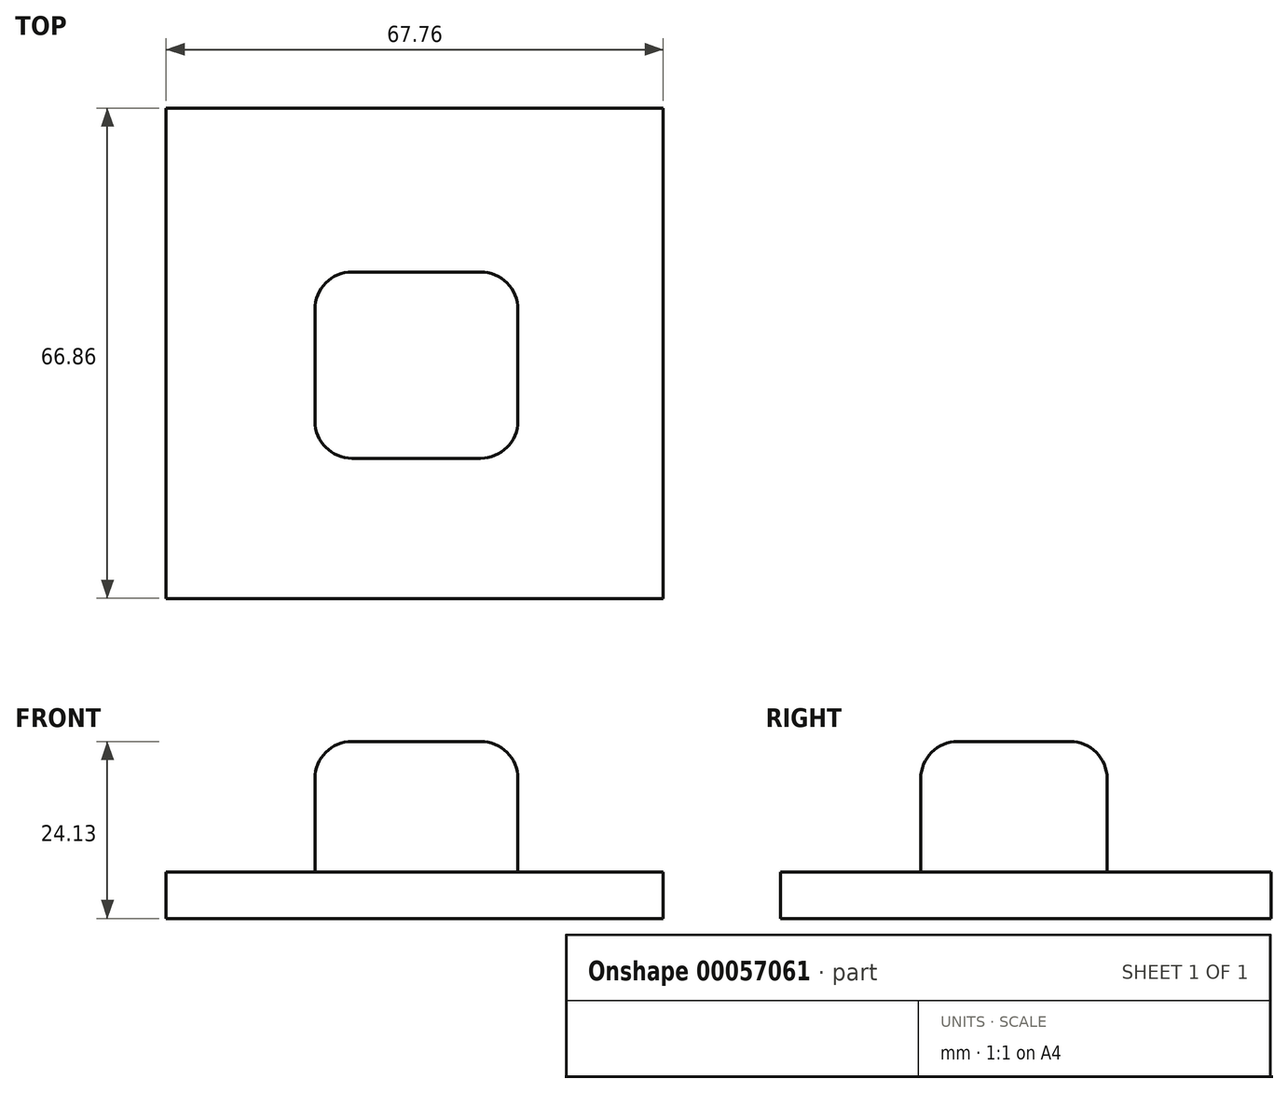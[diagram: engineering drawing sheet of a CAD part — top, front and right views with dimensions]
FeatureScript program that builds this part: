
annotation { "Feature Type Name" : "Feature", "Feature Type Description" : "" }
export const myFeature = defineFeature(function(context is Context, id is Id, definition is map)
    precondition{}
    {
        {
            var Q0;
            Q0=qCreatedBy(makeId("Top.planeOp"),FACE);
            var sketch = newSketch(context, id + "F0", { "sketchPlane" : qUnion([Q0])});
            skLineSegment(sketch, "E0.bottom", {"start": v(-35.63, 22.68) * mm, "end": v(32.13, 22.68) * mm});
            skLineSegment(sketch, "E0.top", {"start": v(-35.63, -44.18) * mm, "end": v(32.13, -44.18) * mm});
            skLineSegment(sketch, "E0.left", {"start": v(-35.63, 22.68) * mm, "end": v(-35.63, -44.18) * mm});
            skLineSegment(sketch, "E0.right", {"start": v(32.13, 22.68) * mm, "end": v(32.13, -44.18) * mm});
            skSolve(sketch);
        }
        {
            var Q0;
            Q0=makeQuery(id+"F0.imprint","IMPRINT",FACE,{"disambiguationData":[TD([[makeQuery(id+"F0.imprint","IMPRINT",EDGE,{"derivedFrom":sQuery(id+"F0.wireOp",EDGE,"E0.bottom")}),-1.0]])]});
            extrude(context, id + "F1", {"entities" : qUnion([Q0]), "depth" : 6.35 * mm});
        }
        {
            var Q0;
            Q0=makeQuery(id+"F1.opExtrude","CAP_FACE",FACE,{"disambiguationData":[OSD([sQuery(id+"F0.wireOp",EDGE,"E0.bottom"),sQuery(id+"F0.wireOp",EDGE,"E0.top"),sQuery(id+"F0.wireOp",EDGE,"E0.left"),sQuery(id+"F0.wireOp",EDGE,"E0.right")])],"isStart":false});
            var sketch = newSketch(context, id + "F2", { "sketchPlane" : qUnion([Q0])});
            skLineSegment(sketch, "E1.bottom", {"start": v(-15.36, 0.31) * mm, "end": v(12.32, 0.31) * mm});
            skLineSegment(sketch, "E1.top", {"start": v(-15.36, -25.09) * mm, "end": v(12.32, -25.09) * mm});
            skLineSegment(sketch, "E1.left", {"start": v(-15.36, 0.31) * mm, "end": v(-15.36, -25.09) * mm});
            skLineSegment(sketch, "E1.right", {"start": v(12.32, 0.31) * mm, "end": v(12.32, -25.09) * mm});
            skSolve(sketch);
        }
        {
            var Q0;
            Q0=makeQuery(id+"F2.imprint","IMPRINT",FACE,{"disambiguationData":[TD([[makeQuery(id+"F2.imprint","IMPRINT",EDGE,{"derivedFrom":sQuery(id+"F2.wireOp",EDGE,"E1.bottom")}),-1.0]])]});
            extrude(context, id + "F3", {"entities" : qUnion([Q0]), "operationType" : NewBodyOperationType.ADD, "depth" : 17.78 * mm});
        }
        {
            var Q0;
            Q0=makeQuery(id+"F3.opExtrude","SWEPT_EDGE",EDGE,{"disambiguationData":[OSD([sQuery(id+"F2.wireOp",EDGE,"E1.top"),sQuery(id+"F2.wireOp",EDGE,"E1.right")])]});
            var Q1;
            Q1=makeQuery(id+"F3.opExtrude","SWEPT_EDGE",EDGE,{"disambiguationData":[OSD([sQuery(id+"F2.wireOp",EDGE,"E1.top"),sQuery(id+"F2.wireOp",EDGE,"E1.left")])]});
            var Q2;
            Q2=makeQuery(id+"F3.opExtrude","SWEPT_EDGE",EDGE,{"disambiguationData":[OSD([sQuery(id+"F2.wireOp",EDGE,"E1.bottom"),sQuery(id+"F2.wireOp",EDGE,"E1.left")])]});
            var Q3;
            Q3=makeQuery(id+"F3.opExtrude","SWEPT_EDGE",EDGE,{"disambiguationData":[OSD([sQuery(id+"F2.wireOp",EDGE,"E1.bottom"),sQuery(id+"F2.wireOp",EDGE,"E1.right")])]});
            fillet(context, id + "F4", {"entities" : qUnion([Q0, Q1, Q2, Q3]), "radius" : 5.08 * mm, "tangentPropagation" : true, "allowEdgeOverflow" : false});
        }
        {
            var Q0;
            Q0=makeQuery(id+"F3.opExtrude","CAP_EDGE",EDGE,{"disambiguationData":[OSD([sQuery(id+"F2.wireOp",EDGE,"E1.top")])],"isStart":false});
            fillet(context, id + "F5", {"entities" : qUnion([Q0]), "radius" : 5.08 * mm, "tangentPropagation" : true, "allowEdgeOverflow" : false});
        }
    });
